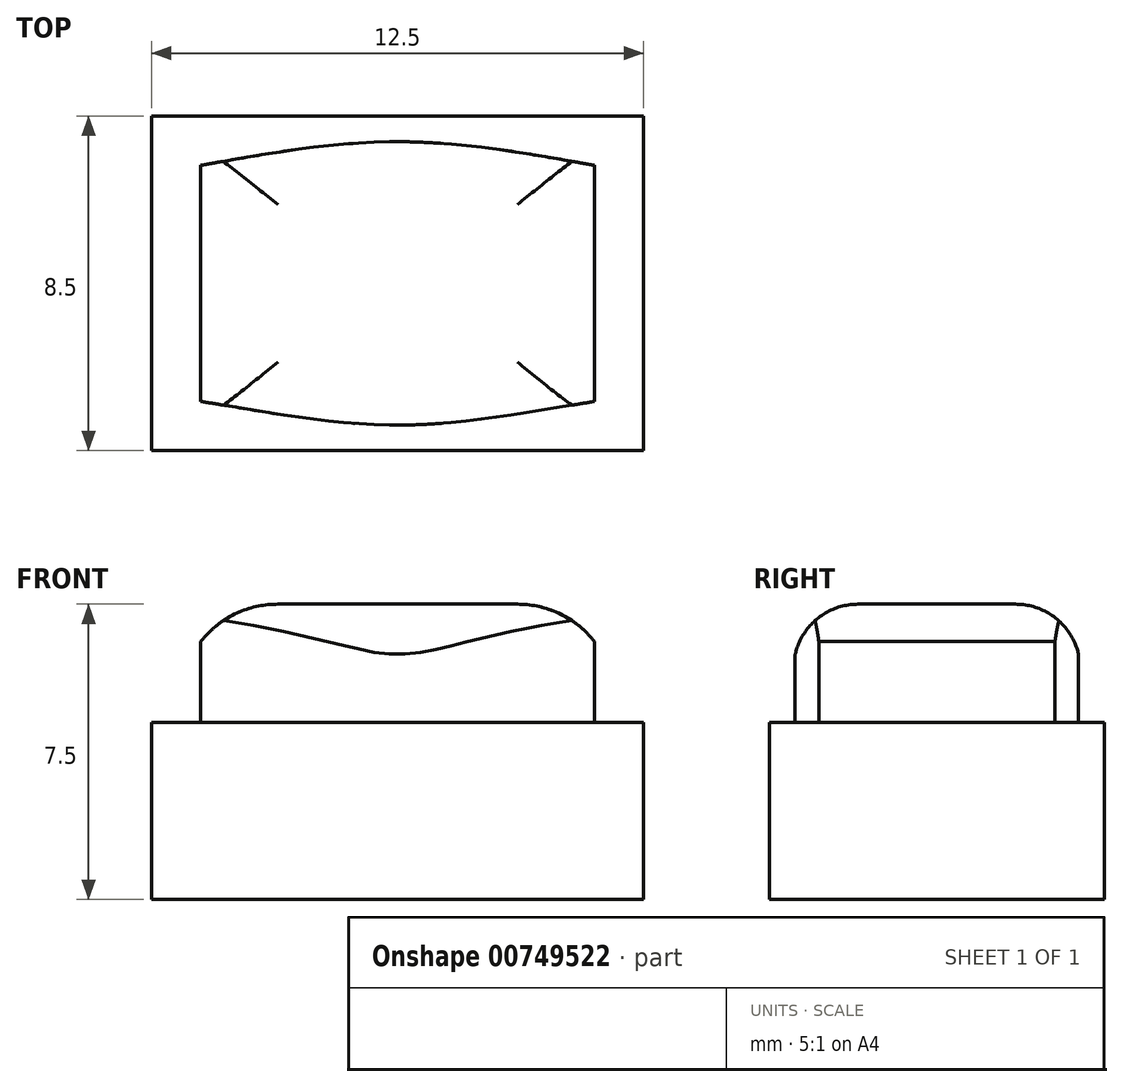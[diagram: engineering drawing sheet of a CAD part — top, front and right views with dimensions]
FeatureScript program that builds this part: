
annotation { "Feature Type Name" : "Feature", "Feature Type Description" : "" }
export const myFeature = defineFeature(function(context is Context, id is Id, definition is map)
    precondition{}
    {
        {
            var Q0;
            Q0=qCreatedBy(makeId("Top.planeOp"),FACE);
            var sketch = newSketch(context, id + "F0", { "sketchPlane" : qUnion([Q0])});
            skLineSegment(sketch, "E0.bottom", {"start": v(-6.25, 4.25) * mm, "end": v(6.25, 4.25) * mm});
            skLineSegment(sketch, "E0.top", {"start": v(-6.25, -4.25) * mm, "end": v(6.25, -4.25) * mm});
            skLineSegment(sketch, "E0.left", {"start": v(-6.25, 4.25) * mm, "end": v(-6.25, -4.25) * mm});
            skLineSegment(sketch, "E0.right", {"start": v(6.25, 4.25) * mm, "end": v(6.25, -4.25) * mm});
            skSolve(sketch);
        }
        {
            var Q0;
            Q0=makeQuery(id+"F0.imprint","IMPRINT",FACE,{"disambiguationData":[TD([[makeQuery(id+"F0.imprint","IMPRINT",EDGE,{"derivedFrom":sQuery(id+"F0.wireOp",EDGE,"E0.bottom")}),-1.0]])]});
            extrude(context, id + "F1", {"entities" : qUnion([Q0]), "depth" : 4.5 * mm, "offsetDistance" : 25 * mm});
        }
        {
            var Q0;
            Q0=makeQuery(id+"F1.opExtrude","CAP_FACE",FACE,{"disambiguationData":[OSD([sQuery(id+"F0.wireOp",EDGE,"E0.bottom"),sQuery(id+"F0.wireOp",EDGE,"E0.top"),sQuery(id+"F0.wireOp",EDGE,"E0.left"),sQuery(id+"F0.wireOp",EDGE,"E0.right")])],"isStart":false});
            var sketch = newSketch(context, id + "F2", { "sketchPlane" : qUnion([Q0])});
            skLineSegment(sketch, "E1.left", {"start": v(-5, 3) * mm, "end": v(-5, -3) * mm});
            skLineSegment(sketch, "E2", {"start": v(5, -3) * mm, "end": v(5, 3) * mm});
            skFitSpline(sketch, "E3", {"points": [v(-5, 3) * mm, v(0, 3.6) * mm, v(5, 3) * mm], "startDerivative": vector(10, 1.79) * mm, "endDerivative": vector(10, -1.79) * mm});
            skFitSpline(sketch, "E4", {"points": [v(-5, -3) * mm, v(0, -3.6) * mm, v(5, -3) * mm], "startDerivative": vector(10, -1.59) * mm, "endDerivative": vector(10, 1.59) * mm});
            skSolve(sketch);
        }
        {
            var Q0;
            Q0=makeQuery(id+"F2.imprint","IMPRINT",FACE,{"disambiguationData":[TD([[makeQuery(id+"F2.imprint","IMPRINT",EDGE,{"derivedFrom":sQuery(id+"F2.wireOp",EDGE,"E1.left")}),1.0]])]});
            extrude(context, id + "F3", {"entities" : qUnion([Q0]), "operationType" : NewBodyOperationType.ADD, "depth" : 3 * mm, "offsetDistance" : 25 * mm});
        }
        {
            var Q0;
            Q0=qCreatedBy(makeId("Front.planeOp"),FACE);
            var sketch = newSketch(context, id + "F4", { "sketchPlane" : qUnion([Q0])});
            skLineSegment(sketch, "E5", {"start": v(-5.04, 7.73) * mm, "end": v(5.04, 7.73) * mm});
            skLineSegment(sketch, "E6", {"start": v(5.04, 7.73) * mm, "end": v(5.04, 6.5) * mm});
            skLineSegment(sketch, "E7", {"start": v(-5.04, 7.73) * mm, "end": v(-5.04, 6.5) * mm});
            skLineSegment(sketch, "E8", {"start": v(-3.04, 7.5) * mm, "end": v(3.04, 7.5) * mm});
            skArc(sketch, "E9", {"start": v(-3.04, 7.5) * mm, "mid": v(-4.16, 7.24) * mm, "end": v(-5.04, 6.5) * mm});
            skArc(sketch, "E10", {"start": v(5.04, 6.5) * mm, "mid": v(4.16, 7.24) * mm, "end": v(3.04, 7.5) * mm});
            skSolve(sketch);
        }
        {
            var Q0;
            Q0=makeQuery(id+"F4.imprint","IMPRINT",FACE,{"disambiguationData":[TD([[makeQuery(id+"F4.imprint","IMPRINT",EDGE,{"derivedFrom":sQuery(id+"F4.wireOp",EDGE,"E5")}),-1.0]])]});
            extrude(context, id + "F5", {"entities" : qUnion([Q0]), "operationType" : NewBodyOperationType.REMOVE, "endBound" : BoundingType.SYMMETRIC, "oppositeDirection" : true, "depth" : 25 * mm, "offsetDistance" : 25 * mm});
        }
        {
            var Q0;
            Q0=qCreatedBy(makeId("Right.planeOp"),FACE);
            var sketch = newSketch(context, id + "F6", { "sketchPlane" : qUnion([Q0])});
            skLineSegment(sketch, "E11", {"start": v(3.64, 7.96) * mm, "end": v(-3.64, 7.96) * mm});
            skLineSegment(sketch, "E12", {"start": v(-3.64, 7.96) * mm, "end": v(-3.64, 6) * mm});
            skLineSegment(sketch, "E13", {"start": v(3.64, 7.96) * mm, "end": v(3.64, 6) * mm});
            skLineSegment(sketch, "E14", {"start": v(2, 7.5) * mm, "end": v(-2, 7.5) * mm});
            skArc(sketch, "E15", {"start": v(3.64, 6) * mm, "mid": v(3.1, 7.07) * mm, "end": v(2, 7.5) * mm});
            skArc(sketch, "E16", {"start": v(-2, 7.5) * mm, "mid": v(-3.1, 7.07) * mm, "end": v(-3.64, 6) * mm});
            skSolve(sketch);
        }
        {
            var Q0;
            Q0=makeQuery(id+"F6.imprint","IMPRINT",FACE,{"disambiguationData":[TD([[makeQuery(id+"F6.imprint","IMPRINT",EDGE,{"derivedFrom":sQuery(id+"F6.wireOp",EDGE,"E11")}),1.0]])]});
            extrude(context, id + "F7", {"entities" : qUnion([Q0]), "operationType" : NewBodyOperationType.REMOVE, "endBound" : BoundingType.SYMMETRIC, "oppositeDirection" : true, "depth" : 25 * mm, "offsetDistance" : 25 * mm});
        }
    });
